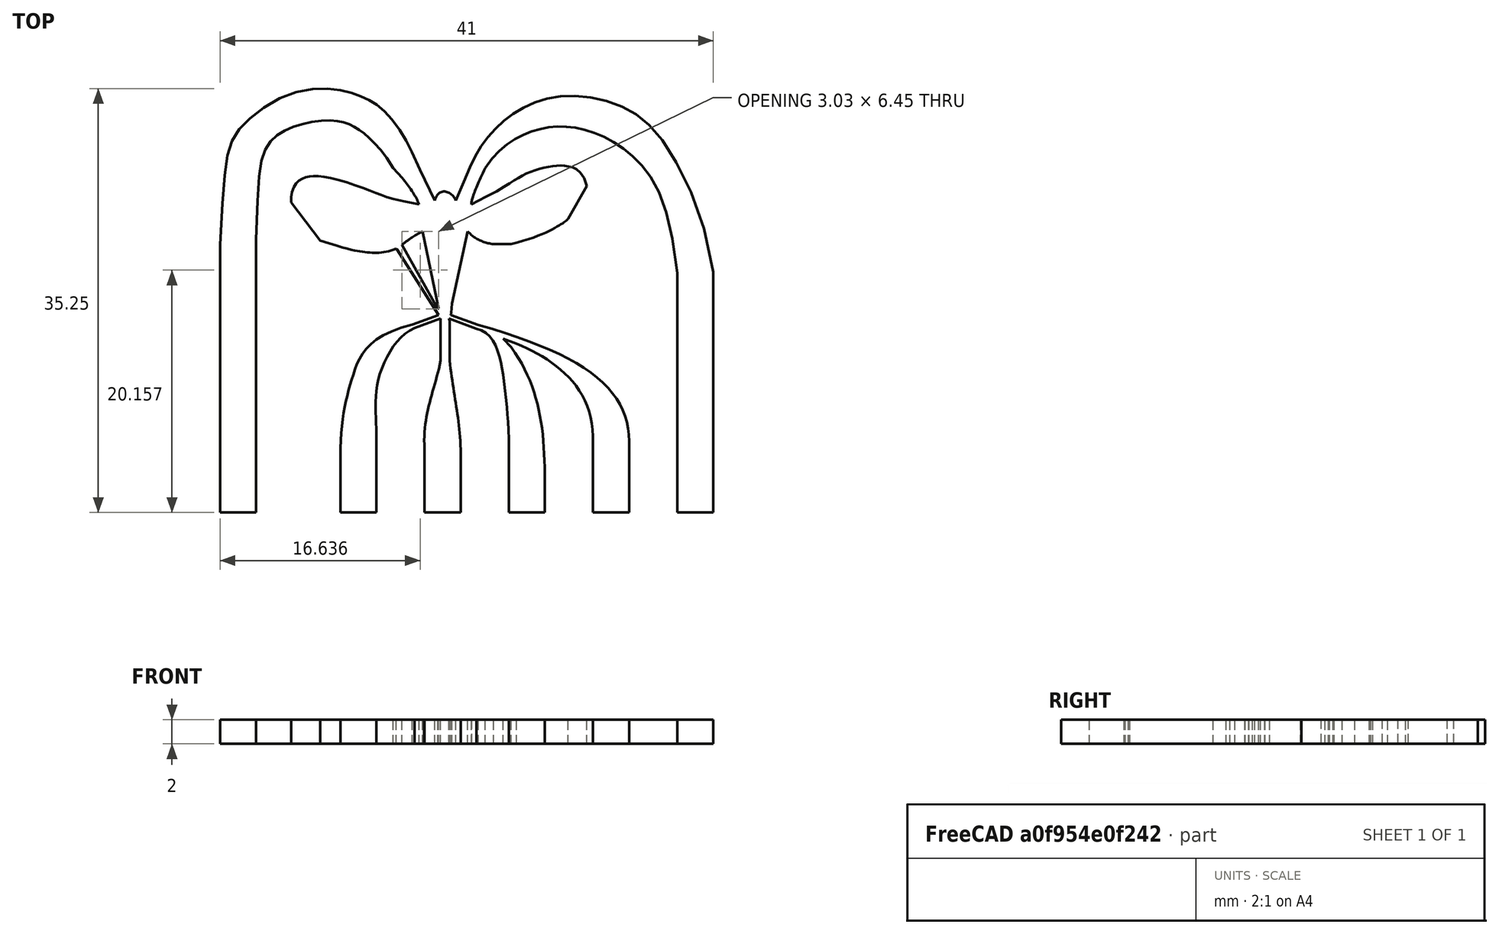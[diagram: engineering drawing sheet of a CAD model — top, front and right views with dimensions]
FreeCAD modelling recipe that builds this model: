
FCSTD DOCUMENT  (FreeCAD 0.20R29177 (Git))
Label: ST41_win3
License: All rights reserved
objects: Part::FeaturePython×7, Sketcher::SketchObject×2, App::DocumentObjectGroupPython×2, PartDesign::Pad×1, PartDesign::Body×1, App::MaterialObjectPython×1
note: 12 computed .brp shape members not serialized (recipe doc carries the construction recipe); baked Part::Feature solids carry a one-line shape summary decoded from their .brp

FEATURE [Sketcher::SketchObject] Sketch
  FullyConstrained = false
  sketch-geometry (2):
    g0: BSplineCurve PolesCount=229 KnotsCount=77 Degree=3 IsPeriodic=0
    g1: BSplineCurve PolesCount=22 KnotsCount=8 Degree=3 IsPeriodic=0
FEATURE [Sketcher::SketchObject] Sketch002
  FullyConstrained = false
  MapMode = 5
  Support = -> [XY_Plane]
  sketch-geometry (251):
    g0: LineSegment StartX=21.2851 StartY=5.29183 StartZ=0 EndX=21.2851 EndY=0 EndZ=0
    g1: LineSegment StartX=21.2851 StartY=0 StartZ=0 EndX=24.2851 EndY=0 EndZ=0
    g2: LineSegment StartX=24.2851 StartY=0 StartZ=0 EndX=24.2851 EndY=5.25113 EndZ=0
    g3: LineSegment StartX=23.3196 StartY=16.1226 StartZ=0 EndX=25.6097 EndY=15.289 EndZ=0
    g4: LineSegment StartX=28.2851 StartY=2.37256 StartZ=0 EndX=28.2851 EndY=0 EndZ=0
    g5: LineSegment StartX=28.2851 StartY=0 StartZ=0 EndX=31.2851 EndY=0 EndZ=0
    g6: LineSegment StartX=31.2851 StartY=0 StartZ=0 EndX=31.2851 EndY=2.04134 EndZ=0
    g7: LineSegment StartX=35.2851 StartY=5.73585 StartZ=0 EndX=35.2851 EndY=0 EndZ=0
    g8: LineSegment StartX=35.2851 StartY=0 StartZ=0 EndX=38.2851 EndY=0 EndZ=0
    g9: LineSegment StartX=38.2851 StartY=0 StartZ=0 EndX=38.2851 EndY=5.9157 EndZ=0
    g10: LineSegment StartX=25.7541 StartY=15.589 StartZ=0 EndX=23.4639 EndY=16.4226 EndZ=0
    g11: LineSegment StartX=42.2851 StartY=19.9202 StartZ=0 EndX=42.2851 EndY=0 EndZ=0
    g12: LineSegment StartX=7.28514 StartY=0 StartZ=0 EndX=7.28514 EndY=22.7104 EndZ=0
    g13: LineSegment StartX=21.1266 StartY=23.3844 StartZ=0 EndX=22.4402 EndY=16.9654 EndZ=0
    g14: LineSegment StartX=22.4402 StartY=16.9654 StartZ=0 EndX=22.3839 EndY=16.9298 EndZ=0
    g15: LineSegment StartX=14.2851 StartY=5.34201 StartZ=0 EndX=14.2851 EndY=0 EndZ=0
    g16: LineSegment StartX=14.2851 StartY=0 StartZ=0 EndX=17.2851 EndY=0 EndZ=0
    g17: LineSegment StartX=17.2851 StartY=0 StartZ=0 EndX=17.2851 EndY=5.5912 EndZ=0
    g18: LineSegment StartX=23.5696 StartY=17.3677 StartZ=0 EndX=24.8766 EndY=23.3844 EndZ=0
    g19: Circle CenterX=26.3326 CenterY=28.642 CenterZ=0 NormalX=0 NormalY=0 NormalZ=1 AngleXU=0 Radius=1
    g20: Circle CenterX=25.1429 CenterY=26.2255 CenterZ=0 NormalX=0 NormalY=0 NormalZ=1 AngleXU=0 Radius=1
    g21: Circle CenterX=25.1766 CenterY=25.6364 CenterZ=0 NormalX=0 NormalY=0 NormalZ=1 AngleXU=0 Radius=1
    g22: BSplineCurve PolesCount=3 KnotsCount=2 Degree=2 IsPeriodic=0
    g23: GeomPoint X=26.3326 Y=28.642 Z=0
    g24: GeomPoint X=25.1766 Y=25.6364 Z=0
    g25-g28: Circle x4 (B-spline internal-alignment scaffolding for g29; pole/knot coordinates omitted)
    g29: BSplineCurve PolesCount=4 KnotsCount=2 Degree=3 IsPeriodic=0
    g30: GeomPoint X=22.1266 Y=25.9297 Z=0
    g31: GeomPoint X=23.8766 Y=25.9297 Z=0
    g32: Circle CenterX=18.6732 CenterY=28.6477 CenterZ=0 NormalX=0 NormalY=0 NormalZ=1 AngleXU=0 Radius=1
    g33: Circle CenterX=20.2619 CenterY=27.0069 CenterZ=0 NormalX=0 NormalY=0 NormalZ=1 AngleXU=0 Radius=1
    g34: Circle CenterX=20.8266 CenterY=25.6364 CenterZ=0 NormalX=0 NormalY=0 NormalZ=1 AngleXU=0 Radius=1
    g35: BSplineCurve PolesCount=3 KnotsCount=2 Degree=2 IsPeriodic=0
    g36: GeomPoint X=18.6732 Y=28.6477 Z=0
    g37: GeomPoint X=20.8266 Y=25.6364 Z=0
    g38-g45: Circle x8 (B-spline internal-alignment scaffolding for g46; pole/knot coordinates omitted)
    g46: BSplineCurve PolesCount=8 KnotsCount=6 Degree=3 IsPeriodic=0
    g47-g52: GeomPoint x6 (B-spline internal-alignment scaffolding for g46; pole/knot coordinates omitted)
    g53: LineSegment StartX=34.7726 StartY=27.1475 StartZ=0 EndX=33.2263 EndY=24.4192 EndZ=0
    g54-g58: Circle x5 (B-spline internal-alignment scaffolding for g59; pole/knot coordinates omitted)
    g59: BSplineCurve PolesCount=5 KnotsCount=3 Degree=3 IsPeriodic=0
    g60: GeomPoint X=28.4711 Y=22.3223 Z=0
    g61: GeomPoint X=32.3947 Y=23.8217 Z=0
    g62: GeomPoint X=33.2263 Y=24.4192 Z=0
    g63: LineSegment StartX=10.1982 StartY=25.7792 StartZ=0 EndX=12.6037 EndY=22.6152 EndZ=0
    g64: BSplineCurve PolesCount=4 KnotsCount=2 Degree=3 IsPeriodic=0
    g65-g74: Circle x10 (B-spline internal-alignment scaffolding for g75; pole/knot coordinates omitted)
    g75: BSplineCurve PolesCount=10 KnotsCount=8 Degree=3 IsPeriodic=0
    g76-g83: GeomPoint x8 (B-spline internal-alignment scaffolding for g75; pole/knot coordinates omitted)
    g84-g93: Circle x10 (B-spline internal-alignment scaffolding for g94; pole/knot coordinates omitted)
    g94: BSplineCurve PolesCount=11 KnotsCount=9 Degree=3 IsPeriodic=0
    g95-g103: GeomPoint x9 (B-spline internal-alignment scaffolding for g94; pole/knot coordinates omitted)
    g104-g114: Circle x11 (B-spline internal-alignment scaffolding for g115; pole/knot coordinates omitted)
    g115: BSplineCurve PolesCount=11 KnotsCount=9 Degree=3 IsPeriodic=0
    g116-g124: GeomPoint x9 (B-spline internal-alignment scaffolding for g115; pole/knot coordinates omitted)
    g125: LineSegment StartX=4.28514 StartY=22.305 StartZ=0 EndX=4.28514 EndY=0 EndZ=0
    g126-g129: Circle x4 (B-spline internal-alignment scaffolding for g130; pole/knot coordinates omitted)
    g130: BSplineCurve PolesCount=4 KnotsCount=2 Degree=3 IsPeriodic=0
    g131: GeomPoint X=27.0191 Y=22.3223 Z=0
    g132: GeomPoint X=24.8766 Y=23.3844 Z=0
    g133-g136: Circle x4 (B-spline internal-alignment scaffolding for g137; pole/knot coordinates omitted)
    g137: BSplineCurve PolesCount=4 KnotsCount=2 Degree=3 IsPeriodic=0
    g138: GeomPoint X=22.6266 Y=12.6418 Z=0
    g139: GeomPoint X=21.2851 Y=5.29183 Z=0
    g140-g143: Circle x4 (B-spline internal-alignment scaffolding for g144; pole/knot coordinates omitted)
    g144: BSplineCurve PolesCount=4 KnotsCount=2 Degree=3 IsPeriodic=0
    g145: GeomPoint X=23.3766 Y=12.6418 Z=0
    g146: GeomPoint X=24.2851 Y=5.25113 Z=0
    g147: LineSegment StartX=4.28514 StartY=0 StartZ=0 EndX=7.28514 EndY=0 EndZ=0
    g148: LineSegment StartX=45.2851 StartY=19.9908 StartZ=0 EndX=45.2851 EndY=0 EndZ=0
    g149: LineSegment StartX=45.2851 StartY=0 StartZ=0 EndX=42.2851 EndY=0 EndZ=0
    g150-g154: Circle x5 (B-spline internal-alignment scaffolding for g155; pole/knot coordinates omitted)
    g155: BSplineCurve PolesCount=5 KnotsCount=3 Degree=3 IsPeriodic=0
    g156: GeomPoint X=28.2851 Y=2.37256 Z=0
    g157: GeomPoint X=27.9196 Y=10.6479 Z=0
    g158: GeomPoint X=25.6097 Y=15.289 Z=0
    g159: LineSegment StartX=22.6116 StartY=16.1226 StartZ=0 EndX=20.4456 EndY=15.3342 EndZ=0
    g160: LineSegment StartX=22.4616 StartY=16.4226 StartZ=0 EndX=20.2708 EndY=15.6252 EndZ=0
    g161-g165: Circle x5 (B-spline internal-alignment scaffolding for g166; pole/knot coordinates omitted)
    g166: BSplineCurve PolesCount=5 KnotsCount=3 Degree=3 IsPeriodic=0
    g167: GeomPoint X=20.4456 Y=15.3342 Z=0
    g168: GeomPoint X=17.3929 Y=10.8039 Z=0
    g169: GeomPoint X=17.2851 Y=5.5912 Z=0
    g170-g174: Circle x5 (B-spline internal-alignment scaffolding for g175; pole/knot coordinates omitted)
    g175: BSplineCurve PolesCount=5 KnotsCount=3 Degree=3 IsPeriodic=0
    g176: GeomPoint X=20.2708 Y=15.6252 Z=0
    g177: GeomPoint X=15.2905 Y=11.2541 Z=0
    g178: GeomPoint X=14.2851 Y=5.34201 Z=0
    g179: LineSegment StartX=27.8226 StartY=14.4514 StartZ=0 EndX=28.4956 EndY=13.7404 EndZ=0
    g180: LineSegment StartX=27.8226 StartY=14.4514 StartZ=0 EndX=28.9347 EndY=14.0467 EndZ=0
    g181-g184: Circle x4 (B-spline internal-alignment scaffolding for g185; pole/knot coordinates omitted)
    g185: BSplineCurve PolesCount=4 KnotsCount=2 Degree=3 IsPeriodic=0
    g186: GeomPoint X=25.7541 Y=15.589 Z=0
    g187: GeomPoint X=38.2851 Y=5.9157 Z=0
    g188-g191: Circle x4 (B-spline internal-alignment scaffolding for g192; pole/knot coordinates omitted)
    g192: BSplineCurve PolesCount=4 KnotsCount=2 Degree=3 IsPeriodic=0
    g193: GeomPoint X=28.9347 Y=14.0467 Z=0
    g194: GeomPoint X=35.2851 Y=5.73585 Z=0
    g195-g198: Circle x4 (B-spline internal-alignment scaffolding for g199; pole/knot coordinates omitted)
    g199: BSplineCurve PolesCount=4 KnotsCount=2 Degree=3 IsPeriodic=0
    g200: GeomPoint X=28.4956 Y=13.7404 Z=0
    g201: GeomPoint X=31.2851 Y=2.04134 Z=0
    g202-g211: Circle x10 (B-spline internal-alignment scaffolding for g212; pole/knot coordinates omitted)
    g212: BSplineCurve PolesCount=10 KnotsCount=8 Degree=3 IsPeriodic=0
    g213-g220: GeomPoint x8 (B-spline internal-alignment scaffolding for g212; pole/knot coordinates omitted)
    g221-g227: Circle x7 (B-spline internal-alignment scaffolding for g228; pole/knot coordinates omitted)
    g228: BSplineCurve PolesCount=7 KnotsCount=5 Degree=3 IsPeriodic=0
    g229-g233: GeomPoint x5 (B-spline internal-alignment scaffolding for g228; pole/knot coordinates omitted)
    g234: LineSegment StartX=22.6116 StartY=16.1226 StartZ=0 EndX=22.6266 EndY=15.9344 EndZ=0
    g235: LineSegment StartX=22.6266 StartY=15.9344 StartZ=0 EndX=22.6266 EndY=12.6418 EndZ=0
    g236: LineSegment StartX=23.3766 StartY=12.6418 StartZ=0 EndX=23.3766 EndY=15.9344 EndZ=0
    g237: LineSegment StartX=23.3766 StartY=15.9344 StartZ=0 EndX=23.3196 EndY=16.1226 EndZ=0
    g238: LineSegment StartX=23.4639 StartY=16.4226 StartZ=0 EndX=23.4864 EndY=16.5964 EndZ=0
    g239: LineSegment StartX=23.5696 StartY=17.3677 StartZ=0 EndX=23.4864 EndY=16.5964 EndZ=0
    g240: LineSegment StartX=27.0191 StartY=22.3223 StartZ=0 EndX=28.4711 EndY=22.3223 EndZ=0
    g241: LineSegment StartX=22.4616 StartY=16.4226 StartZ=0 EndX=18.976 EndY=21.8794 EndZ=0
    g242: LineSegment StartX=22.3839 StartY=16.9298 StartZ=0 EndX=19.412 EndY=22.2492 EndZ=0
    g243: BSplineCurve PolesCount=7 KnotsCount=5 Degree=3 IsPeriodic=0
    g244-g247: Circle x4 (B-spline internal-alignment scaffolding for g64; pole/knot coordinates omitted)
    g248: GeomPoint X=21.1266 Y=23.3844 Z=0
    g249: GeomPoint X=19.412 Y=22.2492 Z=0
    g250: LineSegment StartX=18.976 StartY=21.8794 StartZ=0 EndX=18.9292 EndY=21.9526 EndZ=0
  constraints (248):
    c: PointOnObject(g0,g-1)
    c: Coincident(g0,g1)
    c: PointOnObject(g1,g-1)
    c: Coincident(g1,g2)
    c: Vertical(g2)
    c: PointOnObject(g4,g-1)
    c: Vertical(g4)
    c: Coincident(g4,g5)
    c: PointOnObject(g5,g-1)
    c: Coincident(g5,g6)
    c: PointOnObject(g7,g-1)
    c: Vertical(g7)
    c: Coincident(g7,g8)
    c: PointOnObject(g8,g-1)
    c: Coincident(g8,g9)
    c: Vertical(g9)
    c: PointOnObject(g11,g-1)
    c: Vertical(g11)
    c: PointOnObject(g12,g-1)
    c: Vertical(g12)
    c: Coincident(g13,g14)
    c: PointOnObject(g15,g-1)
    c: Vertical(g15)
    c: Coincident(g15,g16)
    c: PointOnObject(g16,g-1)
    c: Coincident(g16,g17)
    c: Vertical(g17)
    c: Weight(g19) = 1
    c: Equal(g19,g20)
    c: Equal(g19,g21)
    c: InternalAlignment(g19,g22)
    c: InternalAlignment(g20,g22)
    c: InternalAlignment(g21,g22)
    c: InternalAlignment(g23,g22)
    c: InternalAlignment(g24,g22)
    c: Weight(g25) = 1
    c: Equal(g25,g26)
    c: Equal(g25,g27)
    c: Equal(g25,g28)
    c: InternalAlignment(g25-g28 -> g29) x4
    c: InternalAlignment(g30,g29)
    c: InternalAlignment(g31,g29)
    c: Weight(g32) = 1
    c: Equal(g32,g33)
    c: Equal(g32,g34)
    c: InternalAlignment(g32,g35)
    c: InternalAlignment(g33,g35)
    c: InternalAlignment(g34,g35)
    c: InternalAlignment(g36,g35)
    c: InternalAlignment(g37,g35)
    c: Weight(g38) = 1
    c: Equal(g38, g39-g45) x7
    c: InternalAlignment(g38-g45 -> g46) x8
    c: InternalAlignment(g47-g52 -> g46) x6
    c: Coincident(g53,g46)
    c: Weight(g54) = 1
    c: Equal(g54,g55)
    c: Equal(g54,g56)
    c: Equal(g54,g57)
    c: Coincident(g57,g53)
    c: Equal(g54,g58)
    c: Coincident(g59,g53)
    c: InternalAlignment(g54-g58 -> g59) x5
    c: InternalAlignment(g60,g59)
    c: InternalAlignment(g61,g59)
    c: InternalAlignment(g62,g59)
    c: Coincident(g243,g63)
    c: Weight(g65) = 1
    c: Equal(g65, g66-g71) x6
    c: PointOnObject(g71,g70)
    c: Equal(g65,g72)
    c: Equal(g65,g73)
    c: Equal(g65,g74)
    c: Coincident(g75,g63)
    c: InternalAlignment(g65-g74 -> g75) x10
    c: InternalAlignment(g76-g83 -> g75) x8
    c: Weight(g84) = 1
    c: Equal(g84, g85-g93) x9
    c: InternalAlignment(g84-g93 -> g94) x10
    c: InternalAlignment(g95-g103 -> g94) x9
    c: Weight(g104) = 1
    c: Equal(g104, g105-g114) x10
    c: Coincident(g115,g12)
    c: InternalAlignment(g104-g114 -> g115) x11
    c: InternalAlignment(g116-g124 -> g115) x9
    c: Coincident(g125,g94)
    c: Vertical(g125)
    c: Weight(g126) = 1
    c: Equal(g126,g127)
    c: Equal(g126,g128)
    c: Equal(g126,g129)
    c: Coincident(g130,g18)
    c: InternalAlignment(g126-g129 -> g130) x4
    c: InternalAlignment(g131,g130)
    c: InternalAlignment(g132,g130)
    c: Distance(g8) = 3
    c: Distance(g5) = 3
    c: Distance(g1) = 3
    c: Parallel(g2,g0)
    c: Distance(g16) = 3
    c: Parallel(g6,g4)
    c: Weight(g133) = 1
    c: Equal(g133,g134)
    c: Equal(g133,g135)
    c: Equal(g133,g136)
    c: Coincident(g137,g0)
    c: InternalAlignment(g133-g136 -> g137) x4
    c: InternalAlignment(g138,g137)
    c: InternalAlignment(g139,g137)
    c: Weight(g140) = 1
    c: Equal(g140,g141)
    c: Equal(g140,g142)
    c: Equal(g140,g143)
    c: Coincident(g144,g2)
    c: InternalAlignment(g140-g143 -> g144) x4
    c: InternalAlignment(g145,g144)
    c: InternalAlignment(g146,g144)
    c: Coincident(g22,g46)
    c: Coincident(g13,g64)
    c: Coincident(g35,g75)
    c: Coincident(g29,g94)
    c: Coincident(g147,g125)
    c: Coincident(g147,g12)
    c: Horizontal(g147)
    c: Distance(g147) = 3
    c: Distance(g12,g15) = 7
    c: Distance(g1,g4) = 4
    c: Distance(g0,g16) = 4
    c: Distance(g5,g7) = 4
    c: Distance(g8,g11) = 4
    c: DistanceY(g159,g3) = 0
    c: DistanceY(g159,g160) = 0.3
    c: DistanceX(g160,g159) = 0.15
    c: PointOnObject(g148,g-1)
    c: Coincident(g149,g148)
    c: Distance(g149) = 3
    c: Coincident(g11,g149)
    c: Parallel(g10,g3)
    c: Weight(g150) = 1
    c: Coincident(g155,g4)
    c: Equal(g150, g151-g154) x4
    c: Coincident(g155,g3)
    c: InternalAlignment(g150-g154 -> g155) x5
    c: InternalAlignment(g156,g155)
    c: InternalAlignment(g157,g155)
    c: InternalAlignment(g158,g155)
    c: Parallel(g160,g159)
    c: Weight(g161) = 1
    c: Coincident(g166,g159)
    c: Equal(g161, g162-g165) x4
    c: Coincident(g166,g17)
    c: InternalAlignment(g161-g165 -> g166) x5
    c: InternalAlignment(g167,g166)
    c: InternalAlignment(g168,g166)
    c: InternalAlignment(g169,g166)
    c: Weight(g170) = 1
    c: Coincident(g175,g160)
    c: Equal(g170, g171-g174) x4
    c: Coincident(g175,g15)
    c: InternalAlignment(g170-g174 -> g175) x5
    c: InternalAlignment(g176,g175)
    c: InternalAlignment(g177,g175)
    c: InternalAlignment(g178,g175)
    c: Coincident(g180,g179)
    c: Weight(g181) = 1
    c: Coincident(g185,g10)
    c: Equal(g181,g182)
    c: Equal(g181,g183)
    c: Equal(g181,g184)
    c: Coincident(g185,g9)
    c: InternalAlignment(g181-g184 -> g185) x4
    c: InternalAlignment(g186,g185)
    c: InternalAlignment(g187,g185)
    c: Weight(g188) = 1
    c: Coincident(g192,g180)
    c: Equal(g188,g189)
    c: Equal(g188,g190)
    c: Equal(g188,g191)
    c: Coincident(g192,g7)
    c: InternalAlignment(g188-g191 -> g192) x4
    c: InternalAlignment(g193,g192)
    c: InternalAlignment(g194,g192)
    c: Weight(g195) = 1
    c: Coincident(g199,g179)
    c: Equal(g195,g196)
    c: Equal(g195,g197)
    c: Equal(g195,g198)
    c: Coincident(g199,g6)
    c: InternalAlignment(g195-g198 -> g199) x4
    c: InternalAlignment(g200,g199)
    c: InternalAlignment(g201,g199)
    c: Weight(g202) = 1
    c: Coincident(g212,g29)
    c: Equal(g202, g203-g211) x9
    c: Coincident(g212,g148)
    c: InternalAlignment(g202-g211 -> g212) x10
    c: InternalAlignment(g213-g220 -> g212) x8
    c: Weight(g221) = 1
    c: Coincident(g228,g22)
    c: Equal(g221, g222-g227) x6
    c: Coincident(g228,g11)
    c: InternalAlignment(g221-g227 -> g228) x7
    c: InternalAlignment(g229-g233 -> g228) x5
    c: Parallel(g148,g11)
    c: Block(g2)
    c: Block(g0)
    c: Equal(g10,g3)
    c: DistanceY(g35,g22) = 0
    c: DistanceX(g3,g18) = 0.25
    c: Angle(g16,g160) = 0.349066
    c: DistanceY(g13,g18) = 0
    c: Angle(g3,g-1) = 0.349066
    c: DistanceY(g3,g10) = 0.3
    c: Coincident(g159,g234)
    c: Coincident(g234,g235)
    c: Coincident(g235,g137)
    c: Vertical(g235)
    c: Coincident(g236,g144)
    c: Vertical(g236)
    c: Equal(g236,g235)
    c: Distance(g234,g236) = 0.75
    c: DistanceY(g236,g234) = 0
    c: Coincident(g237,g236)
    c: Coincident(g237,g3)
    c: Block(g236)
    c: Block(g235)
    c: Parallel(g3,g180)
    c: DistanceY(g234,g13) = 7.45
    c: DistanceY(g29,g29) = 0
    c: Coincident(g238,g10)
    c: Coincident(g239,g18)
    c: Coincident(g239,g238)
    c: Coincident(g240,g130)
    c: Coincident(g240,g59)
    c: Horizontal(g240)
    c: Coincident(g241,g160)
    c: PointOnObject(g243,g241)
    c: InternalAlignment(g244-g249 -> g64) x6
    c: Coincident(g250,g241)
    c: Coincident(g250,g243)
    c: Coincident(g242,g64)
    c: Coincident(g14,g242)
    c: DistanceX(g236,g18) = 1.5
    c: DistanceX(g13,g234) = 1.5
    c: DistanceX(g13,g29) = 1
    c: DistanceX(g29,g18) = 1
    c: DistanceX(g29,g22) = 1.3
    c: DistanceX(g35,g29) = 1.3
FEATURE [PartDesign::Pad] Pad
  Direction = (0,0,1)
  Length = 2
  Length2 = 100
  Profile = -> Sketch002
  Type = 0
FEATURE [PartDesign::Body] Body
  Group = -> [Sketch,Sketch002,Pad]
  Origin = -> Origin
  Tip = -> Pad
FEATURE [Part::FeaturePython] PhysicsModel  # WARN: FeaturePython — macro-defined, semantics opaque (R4)
  Flow = 0
  Phase = 0
  Thermal = 0
  Time = 0
  Turbulence = 3
  TurbulenceModel = 0
  gx = 0
  gy = -9800
  gz = 0
FEATURE [App::MaterialObjectPython] FluidProperties  # material (typed FeaturePython)
  Category = 1
  Material = CardName=AirIsothermal; Density=1.20 kg/m^3; Description=Standard air properties at 20 Degrees Celsius and 1 atm; DynamicViscosity=1.80e-5 kg/m/s; Name=Air; Type=Isothermal
FEATURE [Part::FeaturePython] InitialiseFields  # WARN: FeaturePython — macro-defined, semantics opaque (R4)
  PotentialFlow = true
  PotentialFlowP = false
  Pressure = 100
  ReThetat = 1
  Temperature = 290
  UseInletTemperatureValue = false
  UseInletTurbulenceValues = false
  UseInletUValues = false
  UseOutletPValue = false
  Ux = 0
  Uy = 0
  Uz = 0
  epsilon = 50000000
  gammaInt = 1
  k = 10000
  kEqnNut = 0
  kEqnk = 10000
  nuTilda = 0
  nut = 0
  omega = 57
FEATURE [Part::FeaturePython] CfdSolver  # WARN: FeaturePython — macro-defined, semantics opaque (R4)
  ConvergenceTol = 0.001
  EndTime = 1
  InputCaseName = case
  MaxIterations = 2000
  Parallel = true
  ParallelCores = 16
  SteadyWriteInterval = 20
  TimeStep = 0
  TransientWriteInterval = 0.05
FEATURE [App::DocumentObjectGroupPython] Pad_Mesh  # scripted group (container) (typed FeaturePython)
  CaseName = meshCase
  CellsBetweenLevels = 3
  CharacteristicLengthMax = 0.075
  ConvertToDualMesh = false
  EdgeRefinement = 1
  ElementDimension = 1
  ImplicitEdgeDetection = false
  MeshUtility = 0
  NumberOfProcesses = 1
  NumberOfThreads = 0
  Part = -> Pad
  PointInMesh = x=29.48816816484 mm; y=26.0 mm; z=0.6 mm
  STLAngularMeshDensity = 100
  STLRelativeLinearDeflection = 1
FEATURE [Part::FeaturePython] CfdFluidBoundary001  label="wall"  # WARN: FeaturePython — macro-defined, semantics opaque (R4)
  BoundarySubType = 0
  BoundaryType = 0
  DefaultBoundary = false
  DissipationRate = 50000000
  HeatFlux = 0
  HeatTransferCoeff = 0
  Intermittency = 1
  MassFlowRate = 0
  NuTilda = 55000000
  PorousBaffleMethod = 0
  Pressure = 0
  PressureDropCoeff = 0
  ReThetat = 1
  ReverseNormal = false
  ScreenSpacing = 2
  ScreenWireDiameter = 0.2
  ShapeRefs = -> [Pad]
  SlipRatio = 0
  SpecificDissipationRate = 57
  Temperature = 290
  ThermalBoundaryType = 0
  TurbulenceInletSpecification = 2
  TurbulenceIntensityPercentage = 1
  TurbulenceLengthScale = 100
  TurbulentKineticEnergy = 10000
  TurbulentViscosity = 50000000
  Ux = 0
  Uy = 0
  Uz = 0
  VelocityIsCartesian = true
  VelocityMag = 0
  VolFlowRate = 0
  kEqnTurbulentKineticEnergy = 10000
  kEqnTurbulentViscosity = 50000000
FEATURE [Part::FeaturePython] CfdFluidBoundary  label="inlet"  # WARN: FeaturePython — macro-defined, semantics opaque (R4)
  BoundarySubType = 9
  BoundaryType = 1
  DefaultBoundary = false
  DirectionFace = CfdFluidBoundary:Face1
  DissipationRate = 50000000
  HeatFlux = 0
  HeatTransferCoeff = 0
  Intermittency = 1
  MassFlowRate = 0
  NuTilda = 55000000
  PorousBaffleMethod = 0
  Pressure = 140
  PressureDropCoeff = 0
  ReThetat = 1
  ReverseNormal = false
  ScreenSpacing = 2
  ScreenWireDiameter = 0.2
  ShapeRefs = -> [Pad]
  SlipRatio = 0
  SpecificDissipationRate = 57
  Temperature = 290
  ThermalBoundaryType = 0
  TurbulenceInletSpecification = 2
  TurbulenceIntensityPercentage = 1
  TurbulenceLengthScale = 100
  TurbulentKineticEnergy = 10000
  TurbulentViscosity = 50000000
  Ux = 0
  Uy = 0
  Uz = 0
  VelocityIsCartesian = false
  VelocityMag = 100
  VolFlowRate = 0
  kEqnTurbulentKineticEnergy = 10000
  kEqnTurbulentViscosity = 50000000
FEATURE [Part::FeaturePython] CfdFluidBoundary002  label="outlet"  # WARN: FeaturePython — macro-defined, semantics opaque (R4)
  BoundarySubType = 10
  BoundaryType = 2
  DefaultBoundary = false
  DissipationRate = 50000000
  HeatFlux = 0
  HeatTransferCoeff = 0
  Intermittency = 1
  MassFlowRate = 0
  NuTilda = 55000000
  PorousBaffleMethod = 0
  Pressure = 0
  PressureDropCoeff = 0
  ReThetat = 1
  ReverseNormal = false
  ScreenSpacing = 2
  ScreenWireDiameter = 0.2
  ShapeRefs = -> [Pad]
  SlipRatio = 0
  SpecificDissipationRate = 57
  Temperature = 290
  ThermalBoundaryType = 0
  TurbulenceInletSpecification = 2
  TurbulenceIntensityPercentage = 1
  TurbulenceLengthScale = 100
  TurbulentKineticEnergy = 10000
  TurbulentViscosity = 50000000
  Ux = 0
  Uy = 0
  Uz = 0
  VelocityIsCartesian = true
  VelocityMag = 0
  VolFlowRate = 0
  kEqnTurbulentKineticEnergy = 10000
  kEqnTurbulentViscosity = 50000000
FEATURE [Part::FeaturePython] CfdFluidBoundary003  label="inlet001"  # WARN: FeaturePython — macro-defined, semantics opaque (R4)
  BoundarySubType = 13
  BoundaryType = 3
  DefaultBoundary = false
  DirectionFace = CfdFluidBoundary003:Face1
  DissipationRate = 50000000
  HeatFlux = 0
  HeatTransferCoeff = 0
  Intermittency = 1
  MassFlowRate = 0
  NuTilda = 55000000
  PorousBaffleMethod = 0
  Pressure = 110
  PressureDropCoeff = 0
  ReThetat = 1
  ReverseNormal = false
  ScreenSpacing = 2
  ScreenWireDiameter = 0.2
  ShapeRefs = -> [Pad]
  SlipRatio = 0
  SpecificDissipationRate = 57
  Temperature = 290
  ThermalBoundaryType = 0
  TurbulenceInletSpecification = 2
  TurbulenceIntensityPercentage = 1
  TurbulenceLengthScale = 100
  TurbulentKineticEnergy = 10000
  TurbulentViscosity = 50000000
  Ux = 0
  Uy = 0
  Uz = 0
  VelocityIsCartesian = false
  VelocityMag = 0
  VolFlowRate = 0
  kEqnTurbulentKineticEnergy = 10000
  kEqnTurbulentViscosity = 50000000
FEATURE [App::DocumentObjectGroupPython] CfdAnalysis  # scripted group (container) (typed FeaturePython)
  Group = -> [PhysicsModel,FluidProperties,InitialiseFields,CfdSolver,Pad_Mesh,CfdFluidBoundary001,CfdFluidBoundary,CfdFluidBoundary002,CfdFluidBoundary003]
  IsActiveAnalysis = true
  NeedsCaseRewrite = false
  NeedsMeshRerun = false
  NeedsMeshRewrite = false
